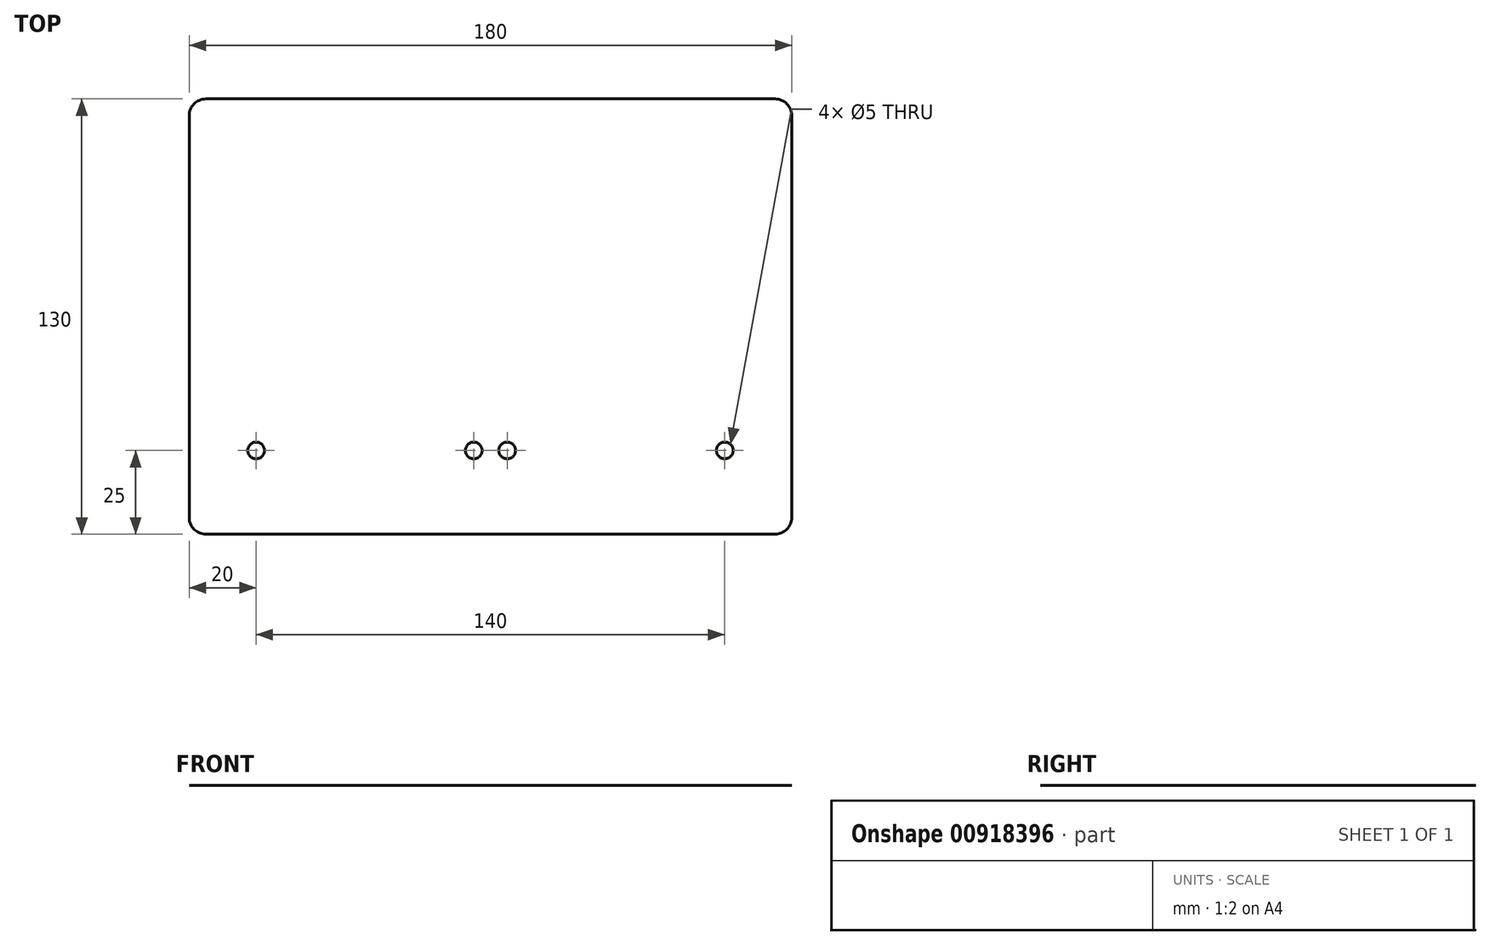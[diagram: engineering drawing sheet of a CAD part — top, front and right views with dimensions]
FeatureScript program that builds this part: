
annotation { "Feature Type Name" : "Feature", "Feature Type Description" : "" }
export const myFeature = defineFeature(function(context is Context, id is Id, definition is map)
    precondition{}
    {
        {
            var Q0;
            Q0=qCreatedBy(makeId("Top.planeOp"),FACE);
            var sketch = newSketch(context, id + "F0", { "sketchPlane" : qUnion([Q0])});
            skLineSegment(sketch, "E0.bottom", {"start": v(90, 65) * mm, "end": v(-90, 65) * mm});
            skLineSegment(sketch, "E0.top", {"start": v(90, -65) * mm, "end": v(-90, -65) * mm});
            skLineSegment(sketch, "E0.left", {"start": v(90, 65) * mm, "end": v(90, -65) * mm});
            skLineSegment(sketch, "E0.right", {"start": v(-90, 65) * mm, "end": v(-90, -65) * mm});
            skPoint(sketch, "E0.middle", {"position": v(0, 0) * mm});
            skLineSegment(sketch, "E1", {"start": v(-90, -40) * mm, "end": v(90, -40) * mm, "construction": true});
            skCircle(sketch, "E2", {"center": v(-70, -40) * mm, "radius": 2.5 * mm});
            skCircle(sketch, "E3", {"center": v(-5, -40) * mm, "radius": 2.5 * mm});
            skCircle(sketch, "E4.MirrorC", {"center": v(70, -40) * mm, "radius": 2.5 * mm});
            skCircle(sketch, "E5.MirrorC", {"center": v(5, -40) * mm, "radius": 2.5 * mm});
            skSolve(sketch);
        }
        {
            var Q0;
            Q0=makeQuery(id+"F0.imprint","IMPRINT",FACE,{"disambiguationData":[TD([[makeQuery(id+"F0.imprint","IMPRINT",EDGE,{"derivedFrom":sQuery(id+"F0.wireOp",EDGE,"E0.bottom")}),1.0]])]});
            extrude(context, id + "F1", {"entities" : qUnion([Q0]), "depth" : 1 / 203.2 * mm, "offsetDistance" : 25 * mm, "symmetric" : true});
        }
        {
            var Q0;
            Q0=makeQuery(id+"F1.opExtrude","SWEPT_EDGE",EDGE,{"disambiguationData":[OSD([sQuery(id+"F0.wireOp",EDGE,"E0.bottom"),sQuery(id+"F0.wireOp",EDGE,"E0.right")])]});
            var Q1;
            Q1=makeQuery(id+"F1.opExtrude","SWEPT_EDGE",EDGE,{"disambiguationData":[OSD([sQuery(id+"F0.wireOp",EDGE,"E0.top"),sQuery(id+"F0.wireOp",EDGE,"E0.right")])]});
            var Q2;
            Q2=makeQuery(id+"F1.opExtrude","SWEPT_EDGE",EDGE,{"disambiguationData":[OSD([sQuery(id+"F0.wireOp",EDGE,"E0.top"),sQuery(id+"F0.wireOp",EDGE,"E0.left")])]});
            var Q3;
            Q3=makeQuery(id+"F1.opExtrude","SWEPT_EDGE",EDGE,{"disambiguationData":[OSD([sQuery(id+"F0.wireOp",EDGE,"E0.bottom"),sQuery(id+"F0.wireOp",EDGE,"E0.left")])]});
            fillet(context, id + "F2", {"entities" : qUnion([Q0, Q1, Q2, Q3]), "radius" : 5 * mm, "tangentPropagation" : true, "allowEdgeOverflow" : false});
        }
    });
